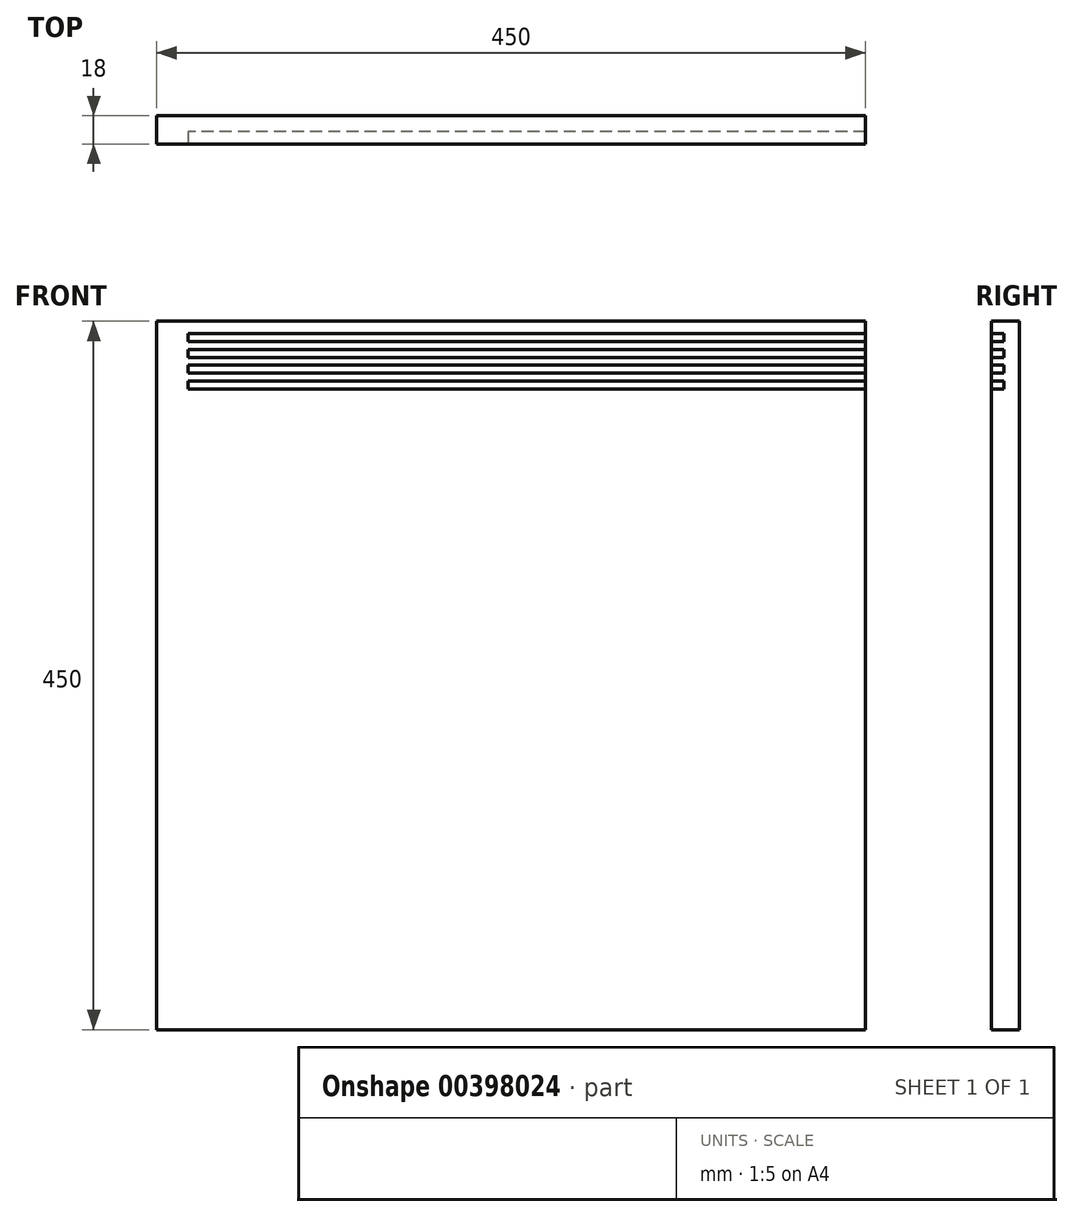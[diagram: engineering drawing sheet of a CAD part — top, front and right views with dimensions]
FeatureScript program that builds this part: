
annotation { "Feature Type Name" : "Feature", "Feature Type Description" : "" }
export const myFeature = defineFeature(function(context is Context, id is Id, definition is map)
    precondition{}
    {
        {
            var Q0;
            Q0=qCreatedBy(makeId("Front.planeOp"),FACE);
            var sketch = newSketch(context, id + "F0", { "sketchPlane" : qUnion([Q0])});
            skLineSegment(sketch, "E0.bottom", {"start": v(225, -225) * mm, "end": v(-225, -225) * mm});
            skLineSegment(sketch, "E0.top", {"start": v(225, 225) * mm, "end": v(-225, 225) * mm});
            skLineSegment(sketch, "E0.left", {"start": v(225, -225) * mm, "end": v(225, 225) * mm});
            skLineSegment(sketch, "E0.right", {"start": v(-225, -225) * mm, "end": v(-225, 225) * mm});
            skPoint(sketch, "E0.middle", {"position": v(0, 0) * mm});
            skSolve(sketch);
        }
        {
            var Q0;
            Q0 = qSketchRegion(id + "F0", true);
            extrude(context, id + "F1", {"entities" : qUnion([Q0]), "oppositeDirection" : true, "depth" : 18 * mm});
        }
        {
            var Q0;
            Q0=makeQuery(id+"F1.opExtrude","CAP_FACE",FACE,{"disambiguationData":[OSD([sQuery(id+"F0.wireOp",EDGE,"E0.bottom"),sQuery(id+"F0.wireOp",EDGE,"E0.top"),sQuery(id+"F0.wireOp",EDGE,"E0.left"),sQuery(id+"F0.wireOp",EDGE,"E0.right")])],"isStart":true});
            var sketch = newSketch(context, id + "F2", { "sketchPlane" : qUnion([Q0])});
            skLineSegment(sketch, "E1.bottom", {"start": v(225, 217) * mm, "end": v(-205, 217) * mm});
            skLineSegment(sketch, "E1.top", {"start": v(225, 212) * mm, "end": v(-205, 212) * mm});
            skLineSegment(sketch, "E1.left", {"start": v(225, 217) * mm, "end": v(225, 212) * mm});
            skLineSegment(sketch, "E1.right", {"start": v(-205, 217) * mm, "end": v(-205, 212) * mm});
            skLineSegment(sketch, "E2.bottom", {"start": v(225, 207) * mm, "end": v(-205, 207) * mm});
            skLineSegment(sketch, "E2.top", {"start": v(225, 202) * mm, "end": v(-205, 202) * mm});
            skLineSegment(sketch, "E2.left", {"start": v(225, 207) * mm, "end": v(225, 202) * mm});
            skLineSegment(sketch, "E2.right", {"start": v(-205, 207) * mm, "end": v(-205, 202) * mm});
            skLineSegment(sketch, "E3.bottom", {"start": v(225, 197) * mm, "end": v(-205, 197) * mm});
            skLineSegment(sketch, "E3.top", {"start": v(225, 192) * mm, "end": v(-205, 192) * mm});
            skLineSegment(sketch, "E3.left", {"start": v(225, 197) * mm, "end": v(225, 192) * mm});
            skLineSegment(sketch, "E3.right", {"start": v(-205, 197) * mm, "end": v(-205, 192) * mm});
            skLineSegment(sketch, "E4.bottom", {"start": v(225, 187) * mm, "end": v(-205, 187) * mm});
            skLineSegment(sketch, "E4.top", {"start": v(225, 182) * mm, "end": v(-205, 182) * mm});
            skLineSegment(sketch, "E4.left", {"start": v(225, 187) * mm, "end": v(225, 182) * mm});
            skLineSegment(sketch, "E4.right", {"start": v(-205, 187) * mm, "end": v(-205, 182) * mm});
            skSolve(sketch);
        }
        {
            var Q0;
            Q0 = qSketchRegion(id + "F2", true);
            extrude(context, id + "F3", {"entities" : qUnion([Q0]), "operationType" : NewBodyOperationType.REMOVE, "oppositeDirection" : true, "depth" : 8 * mm});
        }
    });
